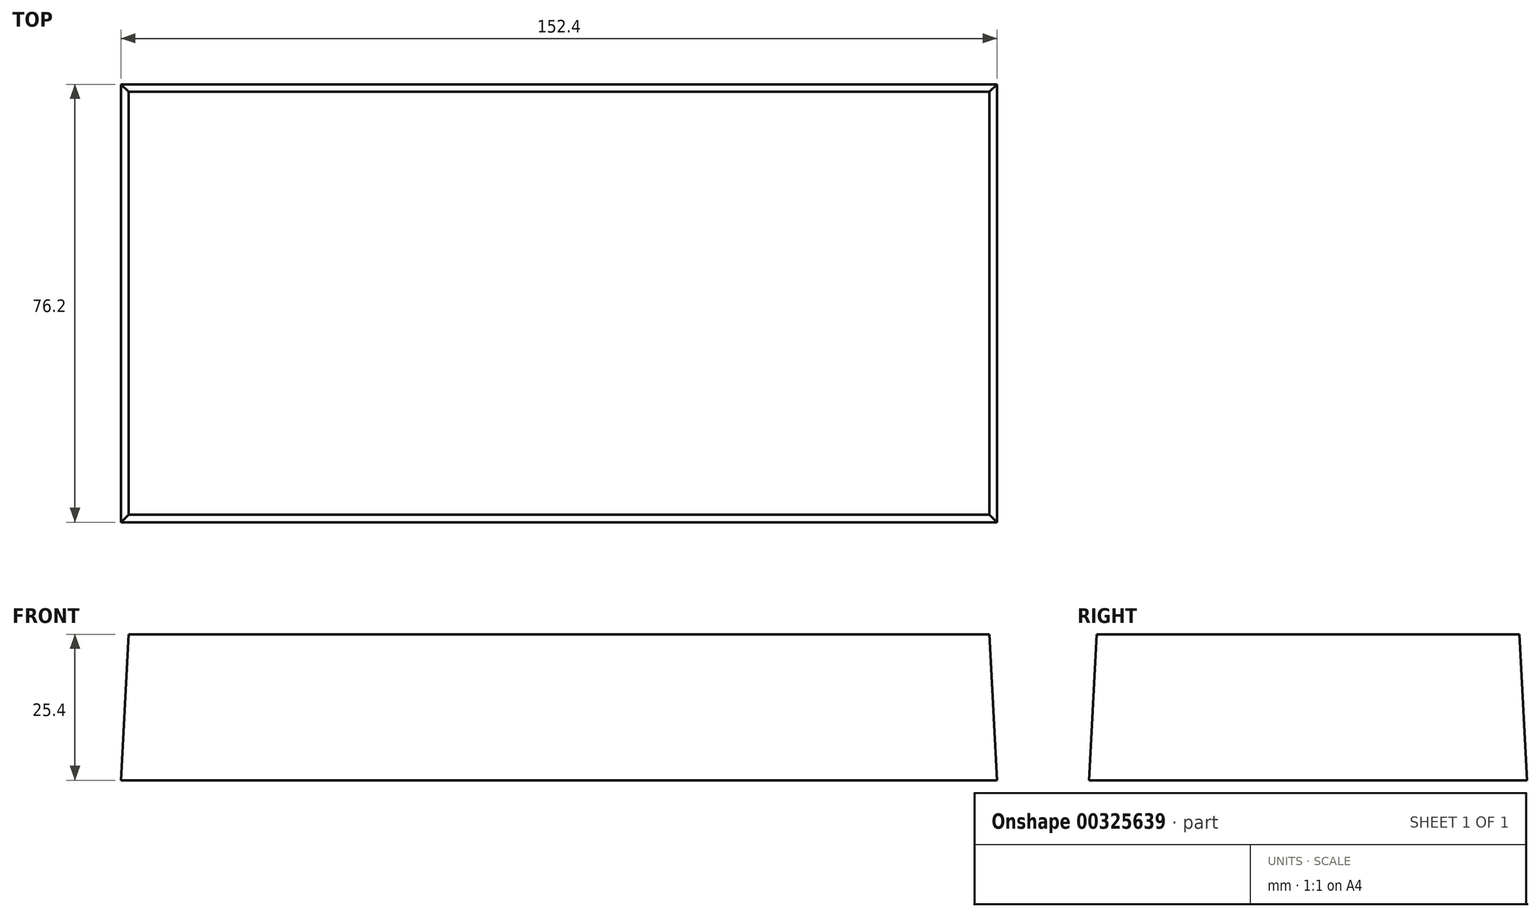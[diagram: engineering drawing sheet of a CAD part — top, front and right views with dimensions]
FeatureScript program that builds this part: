
annotation { "Feature Type Name" : "Feature", "Feature Type Description" : "" }
export const myFeature = defineFeature(function(context is Context, id is Id, definition is map)
    precondition{}
    {
        {
            var Q0;
            Q0=qCreatedBy(makeId("Top.planeOp"),FACE);
            var sketch = newSketch(context, id + "F0", { "sketchPlane" : qUnion([Q0])});
            skLineSegment(sketch, "E0.bottom", {"start": v(-76.2, -38.1) * mm, "end": v(76.2, -38.1) * mm});
            skLineSegment(sketch, "E0.top", {"start": v(-76.2, 38.1) * mm, "end": v(76.2, 38.1) * mm});
            skLineSegment(sketch, "E0.left", {"start": v(-76.2, -38.1) * mm, "end": v(-76.2, 38.1) * mm});
            skLineSegment(sketch, "E0.right", {"start": v(76.2, -38.1) * mm, "end": v(76.2, 38.1) * mm});
            skPoint(sketch, "E0.middle", {"position": v(0, 0) * mm});
            skSolve(sketch);
        }
        {
            var Q0;
            Q0=makeQuery(id+"F0.imprint","IMPRINT",FACE,{"disambiguationData":[TD([[makeQuery(id+"F0.imprint","IMPRINT",EDGE,{"derivedFrom":sQuery(id+"F0.wireOp",EDGE,"E0.bottom")}),1.0]])]});
            extrude(context, id + "F1", {"entities" : qUnion([Q0]), "depth" : 25.4 * mm, "hasDraft" : true, "draftAngle" : 3 * degree, "draftPullDirection" : true});
        }
    });
